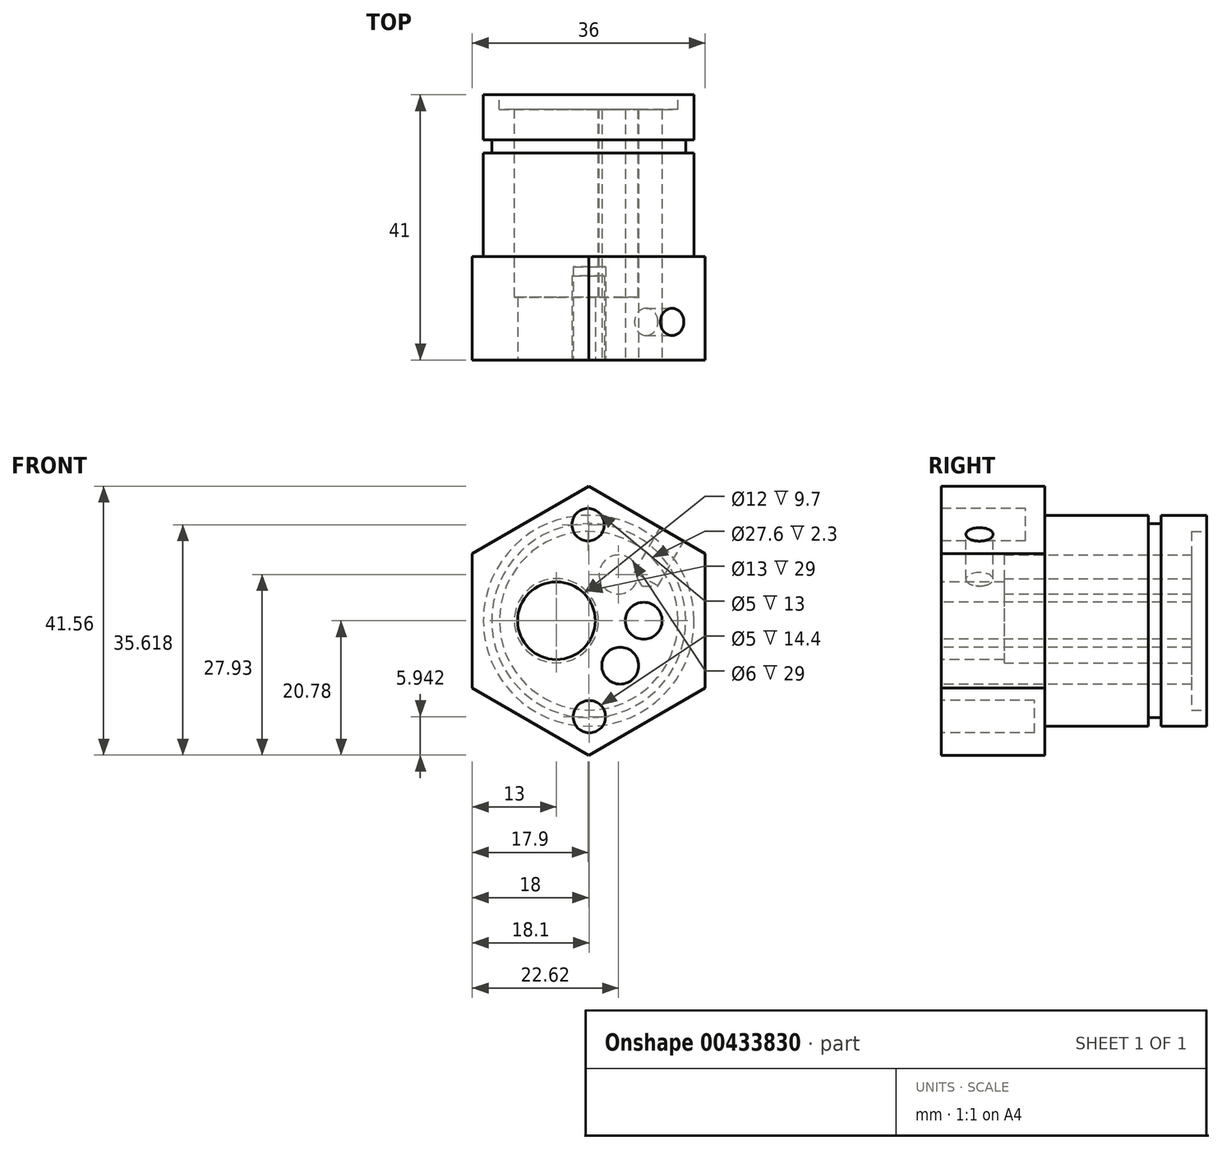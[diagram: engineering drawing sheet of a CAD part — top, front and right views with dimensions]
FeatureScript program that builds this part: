
annotation { "Feature Type Name" : "Feature", "Feature Type Description" : "" }
export const myFeature = defineFeature(function(context is Context, id is Id, definition is map)
    precondition{}
    {
        {
            var Q0;
            Q0=qCreatedBy(makeId("Front.planeOp"),FACE);
            var sketch = newSketch(context, id + "F0", { "sketchPlane" : qUnion([Q0])});
            skCircle(sketch, "E0.cCircle", {"center": v(0, 0) * mm, "radius": 18 * mm, "construction": true});
            skLineSegment(sketch, "E0.0", {"start": v(0, -20.78) * mm, "end": v(-18, -10.4) * mm});
            skLineSegment(sketch, "E0.1", {"start": v(-18, -10.4) * mm, "end": v(-18, 10.4) * mm});
            skLineSegment(sketch, "E0.2", {"start": v(-18, 10.4) * mm, "end": v(0, 20.78) * mm});
            skLineSegment(sketch, "E0.3", {"start": v(0, 20.78) * mm, "end": v(18, 10.4) * mm});
            skLineSegment(sketch, "E0.4", {"start": v(18, 10.4) * mm, "end": v(18, -10.4) * mm});
            skLineSegment(sketch, "E0.5", {"start": v(18, -10.4) * mm, "end": v(0, -20.78) * mm});
            skPoint(sketch, "E0.0.midPoint", {"position": v(-9, -15.59) * mm});
            skSolve(sketch);
        }
        {
            var Q0;
            Q0 = qSketchRegion(id + "F0", true);
            extrude(context, id + "F1", {"entities" : qUnion([Q0]), "oppositeDirection" : true, "depth" : 41 * mm});
        }
        {
            var Q0;
            Q0=makeQuery(id+"F1.opExtrude","CAP_FACE",FACE,{"disambiguationData":[OSD([sQuery(id+"F0.wireOp",EDGE,"E0.0"),sQuery(id+"F0.wireOp",EDGE,"E0.1"),sQuery(id+"F0.wireOp",EDGE,"E0.2"),sQuery(id+"F0.wireOp",EDGE,"E0.3"),sQuery(id+"F0.wireOp",EDGE,"E0.4"),sQuery(id+"F0.wireOp",EDGE,"E0.5")])],"isStart":false});
            var sketch = newSketch(context, id + "F2", { "sketchPlane" : qUnion([Q0])});
            skCircle(sketch, "E1", {"center": v(0, 0) * mm, "radius": 24.47 * mm});
            skCircle(sketch, "E2", {"center": v(0, 0) * mm, "radius": 16.3 * mm});
            skSolve(sketch);
        }
        {
            var Q0;
            Q0 = qSketchRegion(id + "F2", true);
            extrude(context, id + "F3", {"entities" : qUnion([Q0]), "operationType" : NewBodyOperationType.REMOVE, "oppositeDirection" : true, "depth" : 25 * mm});
        }
        {
            var Q0;
            Q0=makeQuery(id+"F1.opExtrude","CAP_FACE",FACE,{"disambiguationData":[OSD([sQuery(id+"F0.wireOp",EDGE,"E0.0"),sQuery(id+"F0.wireOp",EDGE,"E0.1"),sQuery(id+"F0.wireOp",EDGE,"E0.2"),sQuery(id+"F0.wireOp",EDGE,"E0.3"),sQuery(id+"F0.wireOp",EDGE,"E0.4"),sQuery(id+"F0.wireOp",EDGE,"E0.5")])],"isStart":false});
            var sketch = newSketch(context, id + "F4", { "sketchPlane" : qUnion([Q0])});
            skCircle(sketch, "E3", {"center": v(0, 0) * mm, "radius": 21.95 * mm});
            skCircle(sketch, "E4", {"center": v(0, 0) * mm, "radius": 15 * mm});
            skSolve(sketch);
        }
        {
            var Q0;
            Q0 = qSketchRegion(id + "F4", true);
            extrude(context, id + "F5", {"entities" : qUnion([Q0]), "operationType" : NewBodyOperationType.REMOVE, "oppositeDirection" : true, "depth" : 9 * mm});
        }
        {
            var Q0;
            Q0=makeQuery(id+"F1.opExtrude","CAP_FACE",FACE,{"disambiguationData":[OSD([sQuery(id+"F0.wireOp",EDGE,"E0.0"),sQuery(id+"F0.wireOp",EDGE,"E0.1"),sQuery(id+"F0.wireOp",EDGE,"E0.2"),sQuery(id+"F0.wireOp",EDGE,"E0.3"),sQuery(id+"F0.wireOp",EDGE,"E0.4"),sQuery(id+"F0.wireOp",EDGE,"E0.5")])],"isStart":false});
            var sketch = newSketch(context, id + "F6", { "sketchPlane" : qUnion([Q0])});
            skCircle(sketch, "E5", {"center": v(0, 0) * mm, "radius": 16.3 * mm});
            skSolve(sketch);
        }
        {
            var Q0;
            Q0 = qSketchRegion(id + "F6", true);
            extrude(context, id + "F7", {"entities" : qUnion([Q0]), "operationType" : NewBodyOperationType.ADD, "oppositeDirection" : true, "depth" : 7 * mm});
        }
        {
            var Q0;
            Q0=makeQuery(id+"F1.opExtrude","CAP_FACE",FACE,{"disambiguationData":[OSD([sQuery(id+"F0.wireOp",EDGE,"E0.0"),sQuery(id+"F0.wireOp",EDGE,"E0.1"),sQuery(id+"F0.wireOp",EDGE,"E0.2"),sQuery(id+"F0.wireOp",EDGE,"E0.3"),sQuery(id+"F0.wireOp",EDGE,"E0.4"),sQuery(id+"F0.wireOp",EDGE,"E0.5")])],"isStart":true});
            var sketch = newSketch(context, id + "F8", { "sketchPlane" : qUnion([Q0])});
            skCircle(sketch, "E6", {"center": v(8.5, 0) * mm, "radius": 2.85 * mm});
            skCircle(sketch, "E7", {"center": v(4.87, -6.95) * mm, "radius": 2.85 * mm});
            skSolve(sketch);
        }
        {
            var Q0;
            Q0 = qSketchRegion(id + "F8", true);
            extrude(context, id + "F9", {"entities" : qUnion([Q0]), "operationType" : NewBodyOperationType.REMOVE, "endBound" : BoundingType.THROUGH_ALL, "oppositeDirection" : true, "depth" : 25 * mm});
        }
        {
            var Q0;
            Q0=makeQuery(id+"F7.boolean.opBoolean","MERGE",FACE,{"derivedFrom":[makeQuery(id+"F1.opExtrude","CAP_FACE",FACE,{"disambiguationData":[OSD([sQuery(id+"F0.wireOp",EDGE,"E0.0"),sQuery(id+"F0.wireOp",EDGE,"E0.1"),sQuery(id+"F0.wireOp",EDGE,"E0.2"),sQuery(id+"F0.wireOp",EDGE,"E0.3"),sQuery(id+"F0.wireOp",EDGE,"E0.4"),sQuery(id+"F0.wireOp",EDGE,"E0.5")])],"isStart":false}),makeQuery(id+"F7.opExtrude","CAP_FACE",FACE,{"disambiguationData":[OSD([sQuery(id+"F6.wireOp",EDGE,"E5")])],"isStart":true})]});
            var sketch = newSketch(context, id + "F10", { "sketchPlane" : qUnion([Q0])});
            skCircle(sketch, "E8", {"center": v(0, 0) * mm, "radius": 13.8 * mm});
            skSolve(sketch);
        }
        {
            var Q0;
            Q0 = qSketchRegion(id + "F10", true);
            extrude(context, id + "F11", {"entities" : qUnion([Q0]), "operationType" : NewBodyOperationType.REMOVE, "oppositeDirection" : true, "depth" : 2.3 * mm});
        }
        {
            var Q0;
            Q0=makeQuery(id+"F1.opExtrude","CAP_FACE",FACE,{"disambiguationData":[OSD([sQuery(id+"F0.wireOp",EDGE,"E0.0"),sQuery(id+"F0.wireOp",EDGE,"E0.1"),sQuery(id+"F0.wireOp",EDGE,"E0.2"),sQuery(id+"F0.wireOp",EDGE,"E0.3"),sQuery(id+"F0.wireOp",EDGE,"E0.4"),sQuery(id+"F0.wireOp",EDGE,"E0.5")])],"isStart":true});
            var sketch = newSketch(context, id + "F12", { "sketchPlane" : qUnion([Q0])});
            skCircle(sketch, "E9", {"center": v(-5, 0) * mm, "radius": 6 * mm});
            skSolve(sketch);
        }
        {
            var Q0;
            Q0 = qSketchRegion(id + "F12", true);
            extrude(context, id + "F13", {"entities" : qUnion([Q0]), "operationType" : NewBodyOperationType.REMOVE, "endBound" : BoundingType.THROUGH_ALL, "oppositeDirection" : true, "depth" : 25 * mm});
        }
        {
            var Q0;
            Q0=makeQuery(id+"F11.boolean.opBoolean","COPY",FACE,{"derivedFrom":makeQuery(id+"F11.opExtrude","CAP_FACE",FACE,{"disambiguationData":[OSD([sQuery(id+"F10.wireOp",EDGE,"E8")])],"isStart":false})});
            var sketch = newSketch(context, id + "F14", { "sketchPlane" : qUnion([Q0])});
            skCircle(sketch, "E10", {"center": v(5, 0) * mm, "radius": 6.5 * mm});
            skSolve(sketch);
        }
        {
            var Q0;
            Q0 = qSketchRegion(id + "F14", true);
            extrude(context, id + "F15", {"entities" : qUnion([Q0]), "operationType" : NewBodyOperationType.REMOVE, "oppositeDirection" : true, "depth" : 29 * mm});
        }
        {
            var Q0;
            Q0=makeQuery(id+"F1.opExtrude","CAP_FACE",FACE,{"disambiguationData":[OSD([sQuery(id+"F0.wireOp",EDGE,"E0.0"),sQuery(id+"F0.wireOp",EDGE,"E0.1"),sQuery(id+"F0.wireOp",EDGE,"E0.2"),sQuery(id+"F0.wireOp",EDGE,"E0.3"),sQuery(id+"F0.wireOp",EDGE,"E0.4"),sQuery(id+"F0.wireOp",EDGE,"E0.5")])],"isStart":true});
            var sketch = newSketch(context, id + "F16", { "sketchPlane" : qUnion([Q0])});
            skCircle(sketch, "E11", {"center": v(-0.1, 14.84) * mm, "radius": 2.5 * mm});
            skSolve(sketch);
        }
        {
            var Q0;
            Q0 = qSketchRegion(id + "F16", true);
            extrude(context, id + "F17", {"entities" : qUnion([Q0]), "operationType" : NewBodyOperationType.REMOVE, "oppositeDirection" : true, "depth" : 13 * mm});
        }
        {
            var Q0;
            Q0=makeQuery(id+"F1.opExtrude","CAP_FACE",FACE,{"disambiguationData":[OSD([sQuery(id+"F0.wireOp",EDGE,"E0.0"),sQuery(id+"F0.wireOp",EDGE,"E0.1"),sQuery(id+"F0.wireOp",EDGE,"E0.2"),sQuery(id+"F0.wireOp",EDGE,"E0.3"),sQuery(id+"F0.wireOp",EDGE,"E0.4"),sQuery(id+"F0.wireOp",EDGE,"E0.5")])],"isStart":true});
            var sketch = newSketch(context, id + "F18", { "sketchPlane" : qUnion([Q0])});
            skCircle(sketch, "E12", {"center": v(0.1, -14.84) * mm, "radius": 2.5 * mm});
            skSolve(sketch);
        }
        {
            var Q0;
            Q0 = qSketchRegion(id + "F18", true);
            extrude(context, id + "F19", {"entities" : qUnion([Q0]), "operationType" : NewBodyOperationType.REMOVE, "oppositeDirection" : true, "depth" : 14.4 * mm});
        }
        {
            var Q0;
            Q0=makeQuery(id+"F1.opExtrude","SWEPT_FACE",FACE,{"disambiguationData":[OSD([sQuery(id+"F0.wireOp",EDGE,"E0.3")])]});
            var sketch = newSketch(context, id + "F20", { "sketchPlane" : qUnion([Q0])});
            skCircle(sketch, "E13", {"center": v(4.5, 5.9) * mm, "radius": 2.1 * mm});
            skSolve(sketch);
        }
        {
            var Q0;
            Q0=sQuery(id+"F20.wireOp",VERTEX,"E13.center");
            var Q1;
            Q1=makeQuery(id+"F1.opExtrude","SWEPT_BODY",BODY,{"disambiguationData":[OSD([sQuery(id+"F0.wireOp",EDGE,"E0.0"),sQuery(id+"F0.wireOp",EDGE,"E0.1"),sQuery(id+"F0.wireOp",EDGE,"E0.2"),sQuery(id+"F0.wireOp",EDGE,"E0.3"),sQuery(id+"F0.wireOp",EDGE,"E0.4"),sQuery(id+"F0.wireOp",EDGE,"E0.5")])]});
            hole(context, id + "F21", {"style" : HoleStyle.SIMPLE, "endStyle" : HoleEndStyle.BLIND, "holeDiameter" : 4.2 * mm, "holeDepth" : 8 * mm, "isTappedThrough" : true, "tappedDepth" : 12 * mm, "tapClearance" : 3, "locations" : qUnion([Q0]), "scope" : qUnion([Q1])});
        }
        {
            var Q0;
            Q0=makeQuery(id+"F11.boolean.opBoolean","COPY",FACE,{"derivedFrom":makeQuery(id+"F11.opExtrude","CAP_FACE",FACE,{"disambiguationData":[OSD([sQuery(id+"F10.wireOp",EDGE,"E8")])],"isStart":false})});
            var sketch = newSketch(context, id + "F22", { "sketchPlane" : qUnion([Q0])});
            skCircle(sketch, "E14", {"center": v(-4.62, 7.15) * mm, "radius": 3 * mm});
            skPoint(sketch, "E15", {"position": v(-8.5, 0) * mm});
            skSolve(sketch);
        }
        {
            var Q0;
            Q0 = qSketchRegion(id + "F22", true);
            extrude(context, id + "F23", {"entities" : qUnion([Q0]), "operationType" : NewBodyOperationType.REMOVE, "oppositeDirection" : true, "depth" : 29 * mm});
        }
    });
